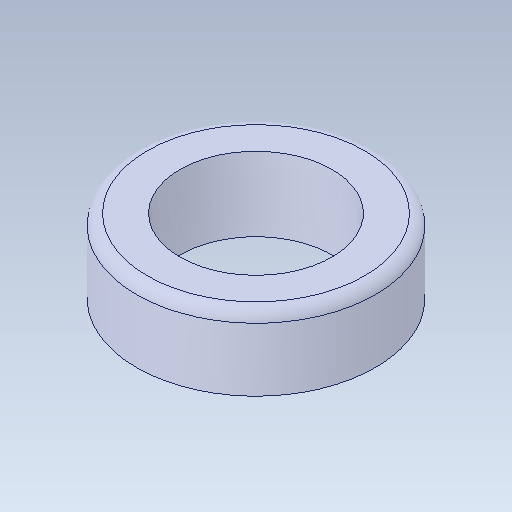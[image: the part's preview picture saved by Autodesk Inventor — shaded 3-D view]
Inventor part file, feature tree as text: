
AUTODESK INVENTOR PART (.ipt)
format: ipt  version: 2020 (Build 240168000, 168)  size: 112,128 bytes
history: mixed  units: mm
features: other x1, fillet x1, imported_body x1
ambient origin geometry x8: Origin, YZ Plane, XZ Plane, XY Plane, X Axis, Y Axis, Z Axis, Center Point
bodies: Body1 (imported_parasolid)
feature tree (3):
  other  "Твердое тело1"
  fillet  "Redondeo1"  [1 undecoded]
  imported_body  NMx_Import_Brep_tag  [imported B-rep: ~5 faces, bbox_mm=[0.0, 3.41, 2.0]]
note: 1 required parameter value undecoded (feature->parameter linkage not recoverable at this tier; creation-order binding heuristic only, values carry confidence <= 0.55)
